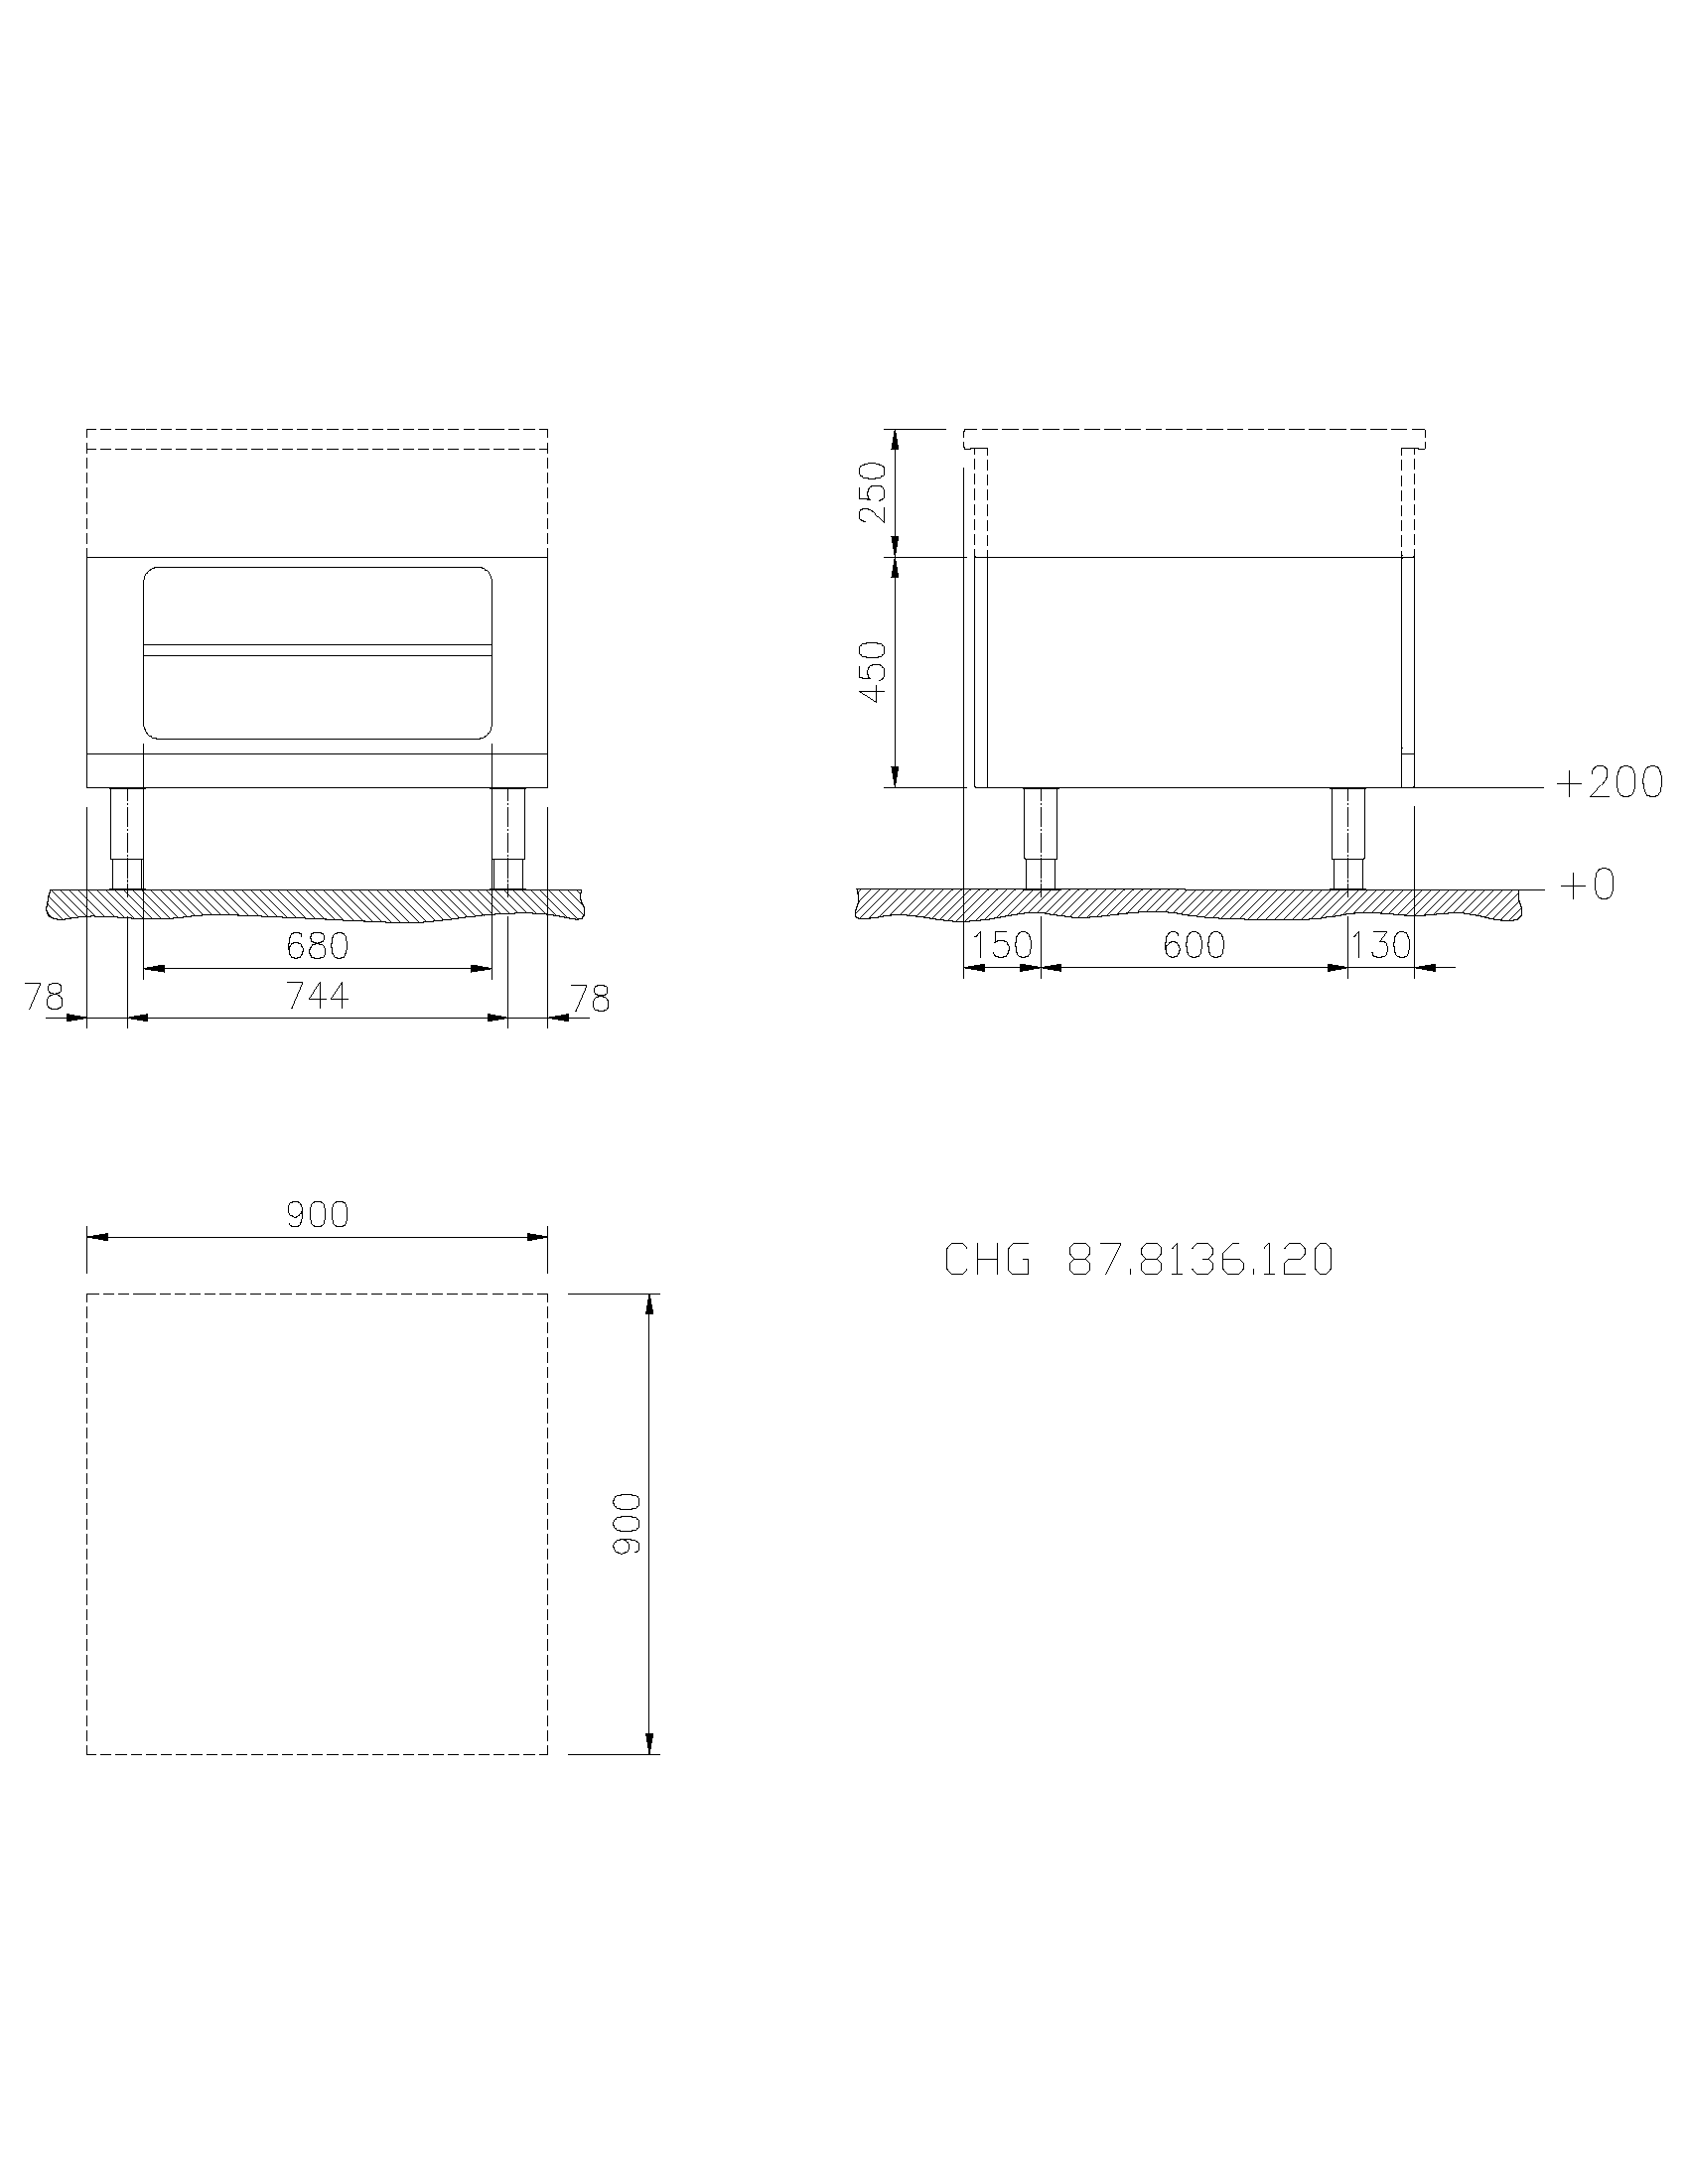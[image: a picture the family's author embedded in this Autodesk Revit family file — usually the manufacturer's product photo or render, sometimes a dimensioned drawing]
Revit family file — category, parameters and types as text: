
# Revit family: QF_ELECTROLUXPROFESSIONAL_589836_MCHXEAD1DM
name_source: partatom
category: Attrezzature speciali
units: mm (PartAtom-declared; Revit-internal decimal feet)

## family parameters
Basato su piano di lavoro = No
Condiviso = No
Punto di calcolo locali = No
Quota connettore circolare = Usa diametro
Sempre verticale = Sì
Taglio con vuoti quando caricato = No
Tipo di parte = Normale

## types (1)
- Standard
    Accessory = Sì
    Cold Water Size = 0"
    Compressed Air Pressure = 0.00 psi
    Compressed Air Size = 0"
    Compressed Air Volume = 0 GPM
    Condensate Return Size = 0"
    Cycle = 50 Hz
    Depth Actual = 900 mm  [stored 2.95276 ft]
    Descrizione = FRYTOP,H3,SMT,1Z,1S,400X900X700H MARINE
    Direct Waste Size = 0"
    Gas Input Pressure = 0.0
    Gas KW = 0
    Gas Size = 0"
    HP = 6.8 HP
    Height Actual = 700 mm  [stored 2.29659 ft]
    Hot Water Size = 0"
    Item Number = 589836
    Length Actual = 400 mm  [stored 1.31234 ft]
    Modello = MCHXEAD1DM
    Phase = 3
    Produttore = Electrolux Professional
    Prospetto di default = 0 mm  [stored 0 ft]
    Refrigerant Compressor Remote = Sì
    Refrigeration Liquid Line Size = 0 mm  [stored 0 ft]
    Refrigeration Suction Line Size = 0 mm  [stored 0 ft]
    Steam Consumption per Hour = 0
    Steam Supply Maximum Pressure = 0.00 psi
    Steam Supply Minimum Pressure = 0.00 psi
    Steam Supply Size = 0"
    URL = https://www.electroluxprofessional.com
    URL Manufacturer = https://www.electroluxprofessional.com
    Volts = 440 V
    Watts = 5100 W
    Weight = 91.00 kg

note: source unit labels omitted for Gas Input Pressure — the stored unit's dimension contradicts the parameter name (converter mislabeling)

note: [stored X ft] marks values corroborated as IEEE doubles in the binary element streams (Revit-internal decimal feet)

## geometry (parser evidence)
native form markers: Blend x14, Sweep x12
no freeform markers — native parametric forms only
